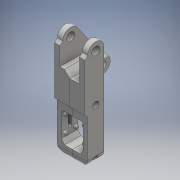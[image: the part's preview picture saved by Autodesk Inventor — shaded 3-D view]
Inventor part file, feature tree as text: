
AUTODESK INVENTOR PART (.ipt)
format: ipt  version: 2016 (Build 200138000, 138)  size: 452,608 bytes
history: native  units: mm
features: sketch x17, extrude x15, chamfer x12, projected_geometry x3, other x2, fillet x2, hole x2, plane x1
ambient origin geometry x8: Origin, YZ Plane, XZ Plane, XY Plane, X Axis, Y Axis, Z Axis, Center Point
bodies: Body1 (feature_tree), Body2 (feature_tree)
feature tree (54):
  other  "Left"
  extrude  "Extrusion8"  Depth=9.0mm
  extrude  "Extrusion9"  Depth=24.3mm
  chamfer  "Chamfer4"  Distance=6.0mm
  extrude  "Extrusion10"  Depth=11.0mm TaperAngle=0.0deg
  fillet  "Fillet1"  Radius=36.0mm
  extrude  "Extrusion11"  TaperAngle=0.0deg  [1 undecoded]
  extrude  "Extrusion12"  Depth=1.0mm TaperAngle=0.0deg
  chamfer  "Chamfer5"  Distance=3.0mm
  extrude  "Extrusion13"  Depth=4.0mm
  hole  "Hole3"  [1 undecoded]
  chamfer  "Chamfer6"  Distance=1.85mm Angle=45.0deg
  extrude  "Extrusion14"  Depth=3.5mm TaperAngle=0.0deg
  chamfer  "Chamfer7"  Distance=1.5mm Angle=45.0deg
  chamfer  "Chamfer8"  Distance=3.25mm Angle=45.0deg
  chamfer  "Chamfer9"  Distance=3.5mm Angle=45.0deg
  plane  "Work Plane1"
  extrude  "Extrusion15"  Depth=1.5mm
  chamfer  "Chamfer10"  Distance=9.0mm
  extrude  "Extrusion16"  Depth=1.5mm TaperAngle=45.0deg
  chamfer  "Chamfer11"  Distance=3.0mm
  extrude  "Extrusion17"  Depth=3.0mm TaperAngle=45.0deg
  extrude  "Extrusion18"  Depth=1.5mm TaperAngle=0.0deg
  extrude  "Extrusion19"  Depth=1.5mm TaperAngle=0.0deg
  extrude  "Extrusion20"  Depth=1.5mm TaperAngle=0.0deg
  chamfer  "Chamfer12"  Distance=3.9mm
  extrude  "Extrusion21"  Depth=1.5mm
  fillet  "Fillet2"  Radius=9.0mm
  hole  "Hole4"  [1 undecoded]
  extrude  "Extrusion22"  Depth=3.0mm TaperAngle=0.0deg
  chamfer  "Chamfer13"  Distance=0.8mm Angle=45.0deg
  chamfer  "Chamfer14"  Distance=3.0mm
  chamfer  "Chamfer15"  Distance=6.5mm
  sketch  "Sketch8"  dims[d64=9.0mm d65=9.0mm]
  sketch  "Sketch9"  dims[d66=34.6mm d67=24.3mm]
  sketch  "Sketch10"  dims[d68=18.0mm]
  sketch  "Sketch11"  dims[d69=18.0mm]
  sketch  "Sketch12"  dims[d70=60.0mm]
  sketch  "Sketch13"  dims[d71=18.0mm d72=6.0mm d73=0.0mm]
  sketch  "Sketch14"  dims[d74=20.0mm d75=11.0mm d76=0.0mm]
  sketch  "Sketch15"  dims[d77=6.0mm d78=2.0mm d79=45.0deg d80=36.0mm]
  sketch  "Sketch16"  dims[d81=9.0mm d82=0.0mm d83=0.0mm]
  sketch  "Sketch17"  dims[d84=6.5mm d85=1.0mm d86=0.0mm]
  sketch  "Sketch18"  dims[d87=3.9mm]
  projected_geometry  "Projected Loop4"
  other  "Right"
  sketch  "Sketch19"  dims[d88=20.0mm d90=18.0mm d91=20.0mm d93=12.0mm]
  projected_geometry  "Projected Loop5"
  sketch  "Sketch20"  dims[d96=3.0mm]
  sketch  "Sketch21"  dims[d97=9.0mm d98=3.0mm d99=0.0mm]
  sketch  "Sketch22"  dims[d100=0.8mm d101=2.0mm d102=45.0deg d103=4.0mm]
  sketch  "Sketch23"  dims[d104=18.0mm d105=3.0mm d106=0.0mm]
  sketch  "Sketch24"  dims[d107=24.0mm d108=3.3mm d109=6.0mm d110=7.0mm d111=9.0mm d112=90.0deg d113=8.0mm d114=20.594885mm d115=1.85mm d116=2.0mm d117=45.0deg d118=3.5mm d119=0.0mm d120=1.5mm d121=2.0mm d122=45.0deg d123=3.25mm d124=4.5mm d125=45.0deg d126=3.5mm d127=4.5mm d128=45.0deg d129=1.0mm d130=9.0mm d131=0.0mm d132=1.0mm d133=4.5mm d134=45.0deg d135=3.0mm d136=0.0mm d137=3.0mm d138=4.5mm d139=45.0deg d140=11.0mm d141=0.0mm d142=6.0mm d143=0.0mm d144=1.0mm d145=0.0mm d146=3.9mm d147=20.0mm d149=18.0mm d150=20.0mm d152=12.0mm d156=9.0mm d157=3.0mm d158=3.0mm d159=0.0mm d160=0.8mm d161=4.5mm d162=45.0deg d163=3.0mm d164=0.0mm d165=6.5mm d166=3.3mm d167=6.0mm d168=7.0mm d169=9.0mm d170=90.0deg d171=8.0mm d172=20.594885mm d173=5.7mm d174=5.7mm d175=2.5mm d176=0.0mm d177=0.64mm d178=4.5mm d179=45.0deg d180=1.5mm d181=4.5mm d182=45.0deg d183=3.25mm d184=4.5mm d185=45.0deg]
  projected_geometry  "Projected Loop6"
note: 3 required parameter values undecoded (feature->parameter linkage not recoverable at this tier; creation-order binding heuristic only, values carry confidence <= 0.55)
